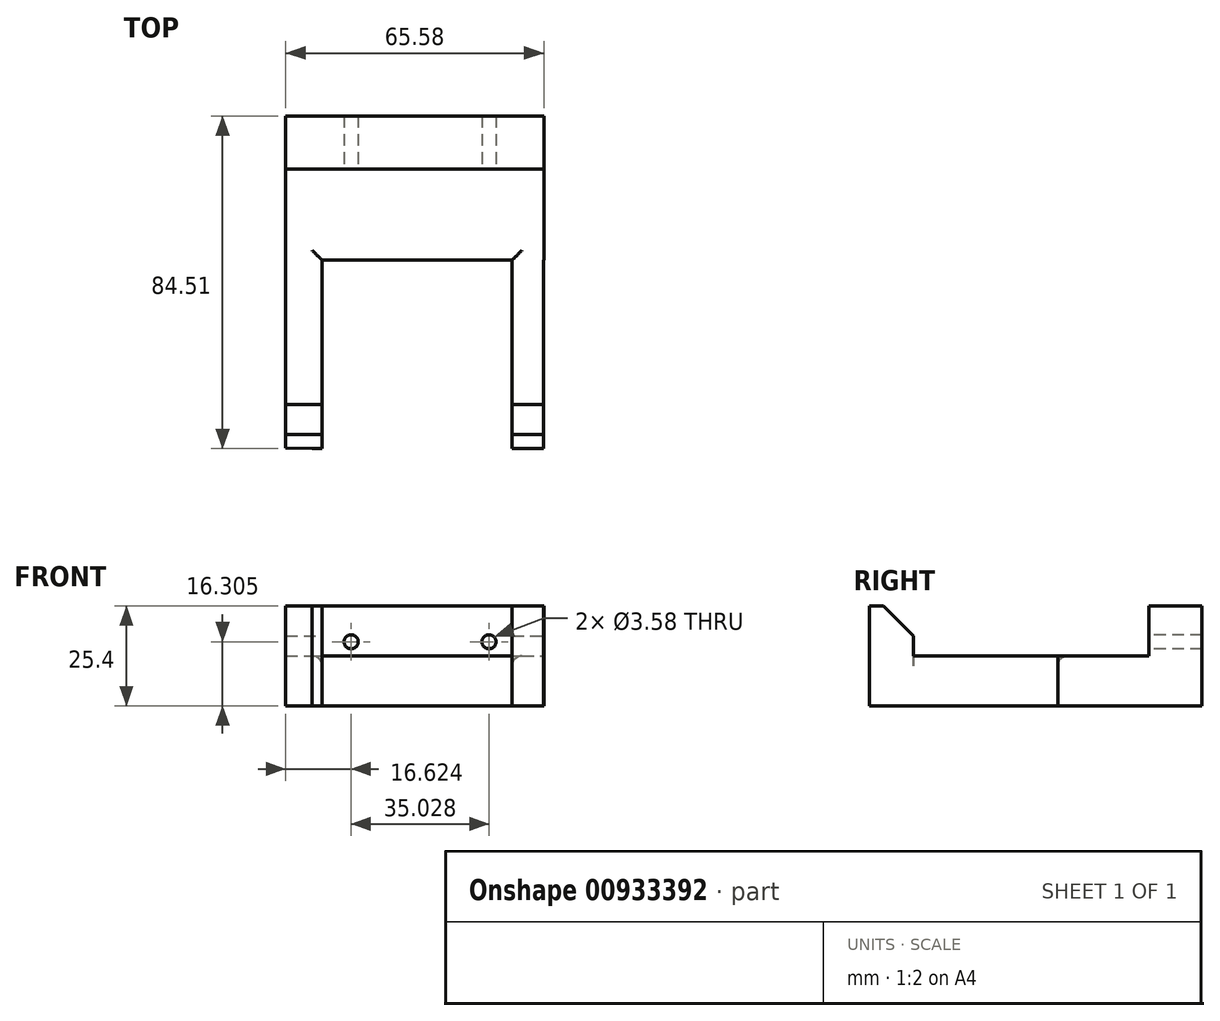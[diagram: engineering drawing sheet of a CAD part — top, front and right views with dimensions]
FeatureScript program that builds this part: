
annotation { "Feature Type Name" : "Feature", "Feature Type Description" : "" }
export const myFeature = defineFeature(function(context is Context, id is Id, definition is map)
    precondition{}
    {
        {
            var Q0;
            Q0=qCreatedBy(makeId("Top.planeOp"),FACE);
            var sketch = newSketch(context, id + "F0", { "sketchPlane" : qUnion([Q0])});
            skLineSegment(sketch, "E0.bottom", {"start": v(-0.25, 18.6) * mm, "end": v(44.72, 18.6) * mm});
            skLineSegment(sketch, "E0.top", {"start": v(-14.06, -29.24) * mm, "end": v(44.72, -29.24) * mm});
            skLineSegment(sketch, "E1", {"start": v(-11.5, 18.6) * mm, "end": v(-0.25, 18.6) * mm});
            skLineSegment(sketch, "E2", {"start": v(-11.5, 18.6) * mm, "end": v(-11.5, -29.24) * mm});
            skLineSegment(sketch, "E3", {"start": v(44.72, 18.6) * mm, "end": v(36.76, 18.6) * mm});
            skLineSegment(sketch, "E4", {"start": v(36.76, 18.6) * mm, "end": v(36.76, -29.24) * mm});
            skLineSegment(sketch, "E5", {"start": v(-11.5, 13.83) * mm, "end": v(36.76, 13.83) * mm});
            skCircle(sketch, "E6", {"center": v(40.6, 13.82) * mm, "radius": 1.27 * mm});
            skCircle(sketch, "E7", {"center": v(12.63, 4.6) * mm, "radius": 2.42 * mm});
            skCircle(sketch, "E8", {"center": v(-16.29, 13.67) * mm, "radius": 1.6 * mm});
            skLineSegment(sketch, "E9", {"start": v(-0.25, 18.6) * mm, "end": v(-20.74, 18.6) * mm});
            skLineSegment(sketch, "E10", {"start": v(-20.74, 18.6) * mm, "end": v(-20.74, -29.1) * mm});
            skLineSegment(sketch, "E11", {"start": v(-20.74, -29.1) * mm, "end": v(-14.06, -29.24) * mm});
            skLineSegment(sketch, "E12", {"start": v(44.72, 18.6) * mm, "end": v(44.72, -29.24) * mm});
            skPoint(sketch, "E13", {"position": v(12.63, 13.83) * mm});
            skLineSegment(sketch, "E14.bottom", {"start": v(-20.74, 18.6) * mm, "end": v(44.84, 18.6) * mm});
            skLineSegment(sketch, "E14.top", {"start": v(-20.74, 55.27) * mm, "end": v(44.84, 55.27) * mm});
            skLineSegment(sketch, "E14.left", {"start": v(-20.74, 18.6) * mm, "end": v(-20.74, 55.27) * mm});
            skLineSegment(sketch, "E14.right", {"start": v(44.84, 18.6) * mm, "end": v(44.84, 55.27) * mm});
            skLineSegment(sketch, "E15", {"start": v(-20.74, 41.76) * mm, "end": v(44.84, 41.76) * mm});
            skLineSegment(sketch, "E16", {"start": v(-20.74, -18.12) * mm, "end": v(44.72, -18.12) * mm});
            skSolve(sketch);
        }
        {
            var Q0;
            {var subQ1=sQuery(id+"F0.wireOp",EDGE,"E1");Q0=makeQuery(id+"F0.imprint","IMPRINT",FACE,{"disambiguationData":[TD([[makeQuery(id+"F0.imprint","IMPRINT",EDGE,{"derivedFrom":subQ1}),1.0]])]});}
            var Q1;
            Q1=makeQuery(id+"F0.imprint","IMPRINT",FACE,{"disambiguationData":[TD([[makeQuery(id+"F0.imprint","IMPRINT",EDGE,{"derivedFrom":sQuery(id+"F0.wireOp",EDGE,"E8")}),-1.0]])]});
            var Q2;
            Q2=makeQuery(id+"F0.imprint","IMPRINT",FACE,{"disambiguationData":[TD([[makeQuery(id+"F0.imprint","IMPRINT",EDGE,{"derivedFrom":sQuery(id+"F0.wireOp",EDGE,"E6")}),-1.0]])]});
            var Q3;
            Q3=makeQuery(id+"F0.imprint","IMPRINT",FACE,{"disambiguationData":[TD([[makeQuery(id+"F0.imprint","IMPRINT",EDGE,{"derivedFrom":sQuery(id+"F0.wireOp",EDGE,"E6")}),1.0]])]});
            var Q4;
            Q4=makeQuery(id+"F0.imprint","IMPRINT",FACE,{"disambiguationData":[TD([[makeQuery(id+"F0.imprint","IMPRINT",EDGE,{"derivedFrom":sQuery(id+"F0.wireOp",EDGE,"E8")}),1.0]])]});
            extrude(context, id + "F1", {"entities" : qUnion([Q0, Q1, Q2, Q3, Q4]), "depth" : 12.7 * mm, "offsetDistance" : 25.4 * mm});
        }
        {
            var Q0;
            {var subQ0=sQuery(id+"F0.wireOp",EDGE,"E11");Q0=makeQuery(id+"F0.imprint","IMPRINT",FACE,{"disambiguationData":[TD([[makeQuery(id+"F0.imprint","IMPRINT",EDGE,{"derivedFrom":subQ0}),1.0]])]});}
            var Q1;
            {var subQ0=sQuery(id+"F0.wireOp",EDGE,"E12");var subQ1=sQuery(id+"F0.wireOp",EDGE,"E0.top");var subQ2=makeQuery(id+"F0.imprint","INTERSECT",VERTEX,{"derivedFrom":[subQ1,subQ0]});Q1=makeQuery(id+"F0.imprint","IMPRINT",FACE,{"disambiguationData":[TD([[makeQuery(id+"F0.imprint","IMPRINT",EDGE,{"disambiguationData":[TD([[subQ2,1.0]])],"derivedFrom":subQ1}),1.0]])]});}
            var Q2;
            {var subQ0=sQuery(id+"F0.wireOp",EDGE,"E14.top");Q2=makeQuery(id+"F0.imprint","IMPRINT",FACE,{"disambiguationData":[TD([[makeQuery(id+"F0.imprint","IMPRINT",EDGE,{"derivedFrom":subQ0}),-1.0]])]});}
            extrude(context, id + "F2", {"entities" : qUnion([Q0, Q1, Q2]), "operationType" : NewBodyOperationType.ADD, "depth" : 25.4 * mm, "offsetDistance" : 25.4 * mm});
        }
        {
            var Q0;
            {var subQ0=sQuery(id+"F0.wireOp",EDGE,"E16");Q0=makeQuery(id+"F2.opExtrude","CAP_EDGE",EDGE,{"disambiguationData":[OSD([subQ0]),TDD([makeQuery(id+"F0.imprint","IMPRINT",EDGE,{"disambiguationData":[TD([[makeQuery(id+"F0.imprint","INTERSECT",VERTEX,{"derivedFrom":[sQuery(id+"F0.wireOp",EDGE,"E2"),subQ0]}),1.0]])],"derivedFrom":subQ0})])],"isStart":false});}
            var Q1;
            {var subQ0=sQuery(id+"F0.wireOp",EDGE,"E16");Q1=makeQuery(id+"F2.opExtrude","CAP_EDGE",EDGE,{"disambiguationData":[OSD([subQ0]),TDD([makeQuery(id+"F0.imprint","IMPRINT",EDGE,{"disambiguationData":[TD([[makeQuery(id+"F0.imprint","INTERSECT",VERTEX,{"derivedFrom":[sQuery(id+"F0.wireOp",EDGE,"E12"),subQ0]}),1.0]])],"derivedFrom":subQ0})])],"isStart":false});}
            chamfer(context, id + "F3", {"entities" : qUnion([Q0, Q1]), "width" : 7.62 * mm, "tangentPropagation" : true});
        }
        {
            var Q0;
            Q0=qCreatedBy(makeId("Front.planeOp"),FACE);
            var sketch = newSketch(context, id + "F4", { "sketchPlane" : qUnion([Q0])});
            skLineSegment(sketch, "E17", {"start": v(30.91, 16.3) * mm, "end": v(-4.12, 16.3) * mm});
            skSolve(sketch);
        }
        {
            var Q0;
            Q0=sQuery(id+"F4.wireOp",VERTEX,"E17.start");
            var Q1;
            Q1=sQuery(id+"F4.wireOp",VERTEX,"E17.end");
            var Q2;
            Q2=makeQuery(id+"F1.opExtrude","SWEPT_BODY",BODY,{"disambiguationData":[OSD([sQuery(id+"F0.wireOp",EDGE,"E0.bottom"),sQuery(id+"F0.wireOp",EDGE,"E1"),sQuery(id+"F0.wireOp",EDGE,"E2"),sQuery(id+"F0.wireOp",EDGE,"E4"),sQuery(id+"F0.wireOp",EDGE,"E10"),sQuery(id+"F0.wireOp",EDGE,"E12"),sQuery(id+"F0.wireOp",EDGE,"E14.bottom"),sQuery(id+"F0.wireOp",EDGE,"E14.left"),sQuery(id+"F0.wireOp",EDGE,"E14.right"),sQuery(id+"F0.wireOp",EDGE,"E15"),sQuery(id+"F0.wireOp",EDGE,"E16")])]});
            hole(context, id + "F5", {"style" : HoleStyle.SIMPLE, "endStyle" : HoleEndStyle.THROUGH, "holeDiameter" : 3.58 * mm, "majorDiameter" : 6.35 * mm, "isTappedThrough" : true, "tappedDepth" : 12.7 * mm, "tapClearance" : 3, "locations" : qUnion([Q0, Q1]), "scope" : qUnion([Q2])});
        }
        {
            var Q0;
            Q0=makeQuery(id+"F1.opExtrude","CAP_EDGE",EDGE,{"disambiguationData":[OSD([sQuery(id+"F0.wireOp",EDGE,"E2")])],"isStart":false});
            var Q1;
            Q1=makeQuery(id+"F1.opExtrude","CAP_EDGE",EDGE,{"disambiguationData":[OSD([sQuery(id+"F0.wireOp",EDGE,"E0.bottom"),sQuery(id+"F0.wireOp",EDGE,"E1")])],"isStart":false});
            var Q2;
            Q2=makeQuery(id+"F1.opExtrude","CAP_EDGE",EDGE,{"disambiguationData":[OSD([sQuery(id+"F0.wireOp",EDGE,"E4")])],"isStart":false});
            fillet(context, id + "F6", {"entities" : qUnion([Q0, Q1, Q2]), "radius" : 2.54 * mm, "tangentPropagation" : true, "allowEdgeOverflow" : false});
        }
    });
